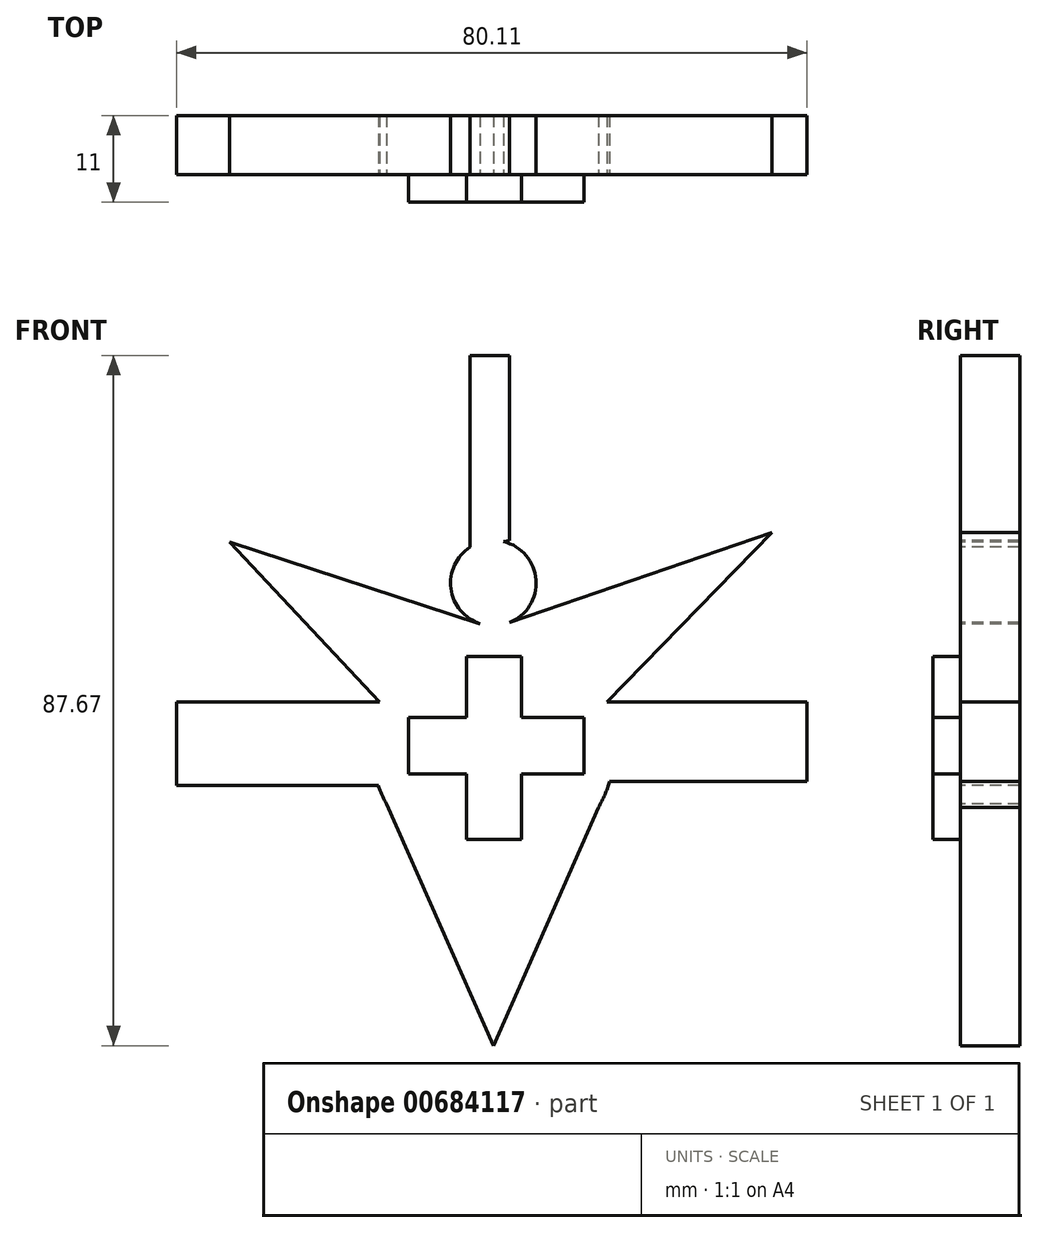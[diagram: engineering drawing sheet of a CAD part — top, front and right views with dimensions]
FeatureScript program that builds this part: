
annotation { "Feature Type Name" : "Feature", "Feature Type Description" : "" }
export const myFeature = defineFeature(function(context is Context, id is Id, definition is map)
    precondition{}
    {
        {
            var Q0;
            Q0=qCreatedBy(makeId("Front.planeOp"),FACE);
            var sketch = newSketch(context, id + "F0", { "sketchPlane" : qUnion([Q0])});
            skCircle(sketch, "E0", {"center": v(0, 0) * mm, "radius": 15.46 * mm});
            skSolve(sketch);
        }
        {
            var Q0;
            Q0=makeQuery(id+"F0.imprint","IMPRINT",FACE,{"disambiguationData":[TD([[makeQuery(id+"F0.imprint","IMPRINT",EDGE,{"derivedFrom":sQuery(id+"F0.wireOp",EDGE,"E0")}),1.0]])]});
            extrude(context, id + "F1", {"entities" : qUnion([Q0]), "oppositeDirection" : true, "depth" : 7.5 * mm, "offsetDistance" : 25 * mm});
        }
        {
            var Q0;
            Q0=qCreatedBy(makeId("Front.planeOp"),FACE);
            var sketch = newSketch(context, id + "F2", { "sketchPlane" : qUnion([Q0])});
            skLineSegment(sketch, "E1.bottom", {"start": v(-3.4, 11.35) * mm, "end": v(3.59, 11.35) * mm});
            skLineSegment(sketch, "E1.top", {"start": v(-3.4, -11.93) * mm, "end": v(3.59, -11.93) * mm});
            skLineSegment(sketch, "E1.left", {"start": v(-3.4, 11.35) * mm, "end": v(-3.4, 3.59) * mm});
            skLineSegment(sketch, "E1.right", {"start": v(3.59, 11.35) * mm, "end": v(3.59, 3.59) * mm});
            skLineSegment(sketch, "E2.bottom", {"start": v(-10.77, 3.59) * mm, "end": v(-3.4, 3.59) * mm});
            skLineSegment(sketch, "E2.top", {"start": v(-10.77, -3.59) * mm, "end": v(-3.4, -3.59) * mm});
            skLineSegment(sketch, "E2.left", {"start": v(-10.77, 3.59) * mm, "end": v(-10.77, -3.59) * mm});
            skLineSegment(sketch, "E2.right", {"start": v(11.54, 3.59) * mm, "end": v(11.54, -3.59) * mm});
            skLineSegment(sketch, "E3.trimOffspring", {"start": v(3.59, 3.59) * mm, "end": v(11.54, 3.59) * mm});
            skLineSegment(sketch, "E4.trimOffspring", {"start": v(-3.4, -3.59) * mm, "end": v(-3.4, -11.93) * mm});
            skLineSegment(sketch, "E5.trimOffspring", {"start": v(3.59, -3.59) * mm, "end": v(11.54, -3.59) * mm});
            skLineSegment(sketch, "E6.trimOffspring", {"start": v(3.59, -3.59) * mm, "end": v(3.59, -11.93) * mm});
            skSolve(sketch);
        }
        {
            var Q0;
            Q0 = qSketchRegion(id + "F2", true);
            extrude(context, id + "F3", {"entities" : qUnion([Q0]), "operationType" : NewBodyOperationType.ADD, "depth" : 3.5 * mm, "offsetDistance" : 25 * mm});
        }
        {
            var Q0;
            Q0=makeQuery(id+"F1.opExtrude","CAP_FACE",FACE,{"disambiguationData":[OSD([sQuery(id+"F0.wireOp",EDGE,"E0")])],"isStart":true});
            var sketch = newSketch(context, id + "F4", { "sketchPlane" : qUnion([Q0])});
            skLineSegment(sketch, "E7", {"start": v(-14.61, -5.06) * mm, "end": v(-40.25, -5.06) * mm});
            skLineSegment(sketch, "E8", {"start": v(-40.25, -5.06) * mm, "end": v(-40.25, 5.53) * mm});
            skLineSegment(sketch, "E9", {"start": v(-40.25, 5.53) * mm, "end": v(-14.44, 5.53) * mm});
            skSolve(sketch);
        }
        {
            var Q0;
            Q0 = qSketchRegion(id + "F4", true);
            var Q1;
            {var subQ0=sQuery(id+"F4.wireOp",EDGE,"E7");Q1=makeQuery(id+"F4.imprint","IMPRINT",FACE,{"disambiguationData":[TD([[makeQuery(id+"F4.imprint","IMPRINT",EDGE,{"derivedFrom":subQ0}),-1.0]])]});}
            extrude(context, id + "F5", {"entities" : qUnion([Q0, Q1]), "operationType" : NewBodyOperationType.ADD, "oppositeDirection" : true, "depth" : 7.5 * mm, "offsetDistance" : 25 * mm});
        }
        {
            var Q0;
            {var subQ0=sQuery(id+"F0.wireOp",EDGE,"E0");Q0=makeQuery(id+"F5.boolean.opBoolean","MERGE",FACE,{"derivedFrom":[makeQuery(id+"F1.opExtrude","CAP_FACE",FACE,{"disambiguationData":[OSD([subQ0])],"isStart":true}),makeQuery(id+"F5.opExtrude","CAP_FACE",FACE,{"disambiguationData":[OSD([subQ0,sQuery(id+"F4.wireOp",EDGE,"E7"),sQuery(id+"F4.wireOp",EDGE,"E8"),sQuery(id+"F4.wireOp",EDGE,"E9")])],"isStart":true})]});}
            var sketch = newSketch(context, id + "F6", { "sketchPlane" : qUnion([Q0])});
            skLineSegment(sketch, "E10", {"start": v(14.44, 5.53) * mm, "end": v(39.86, 5.53) * mm});
            skLineSegment(sketch, "E11", {"start": v(39.86, 5.53) * mm, "end": v(39.86, -4.56) * mm});
            skLineSegment(sketch, "E12", {"start": v(40.25, -4.56) * mm, "end": v(14.78, -4.56) * mm});
            skSolve(sketch);
        }
        {
            var Q0;
            Q0 = qSketchRegion(id + "F6", true);
            var Q1;
            {var subQ0=sQuery(id+"F6.wireOp",EDGE,"E10");Q1=makeQuery(id+"F6.imprint","IMPRINT",FACE,{"disambiguationData":[TD([[makeQuery(id+"F6.imprint","IMPRINT",EDGE,{"derivedFrom":subQ0}),-1.0]])]});}
            extrude(context, id + "F7", {"entities" : qUnion([Q0, Q1]), "operationType" : NewBodyOperationType.ADD, "oppositeDirection" : true, "depth" : 7.5 * mm, "offsetDistance" : 25 * mm});
        }
        {
            var Q0;
            {var subQ0=sQuery(id+"F0.wireOp",EDGE,"E0");Q0=makeQuery(id+"F7.boolean.opBoolean","MERGE",FACE,{"derivedFrom":[makeQuery(id+"F5.boolean.opBoolean","MERGE",FACE,{"derivedFrom":[makeQuery(id+"F1.opExtrude","CAP_FACE",FACE,{"disambiguationData":[OSD([subQ0])],"isStart":true}),makeQuery(id+"F5.opExtrude","CAP_FACE",FACE,{"disambiguationData":[OSD([subQ0,sQuery(id+"F4.wireOp",EDGE,"E7"),sQuery(id+"F4.wireOp",EDGE,"E8"),sQuery(id+"F4.wireOp",EDGE,"E9")])],"isStart":true})]}),makeQuery(id+"F7.opExtrude","CAP_FACE",FACE,{"disambiguationData":[OSD([subQ0,sQuery(id+"F6.wireOp",EDGE,"E10"),sQuery(id+"F6.wireOp",EDGE,"E11"),sQuery(id+"F6.wireOp",EDGE,"E12")])],"isStart":true})]});}
            var sketch = newSketch(context, id + "F8", { "sketchPlane" : qUnion([Q0])});
            skLineSegment(sketch, "E13", {"start": v(-14.61, -5.06) * mm, "end": v(0, -38.11) * mm});
            skLineSegment(sketch, "E14", {"start": v(0, -38.11) * mm, "end": v(14.78, -4.56) * mm});
            skSolve(sketch);
        }
        {
            var Q0;
            {var subQ0=sQuery(id+"F8.wireOp",EDGE,"E14");var subQ1=sQuery(id+"F8.wireOp",EDGE,"E13");var subQ2=makeQuery(id+"F8.imprint","INTERSECT",VERTEX,{"derivedFrom":[subQ1,subQ0]});Q0=makeQuery(id+"F8.imprint","IMPRINT",FACE,{"disambiguationData":[TD([[makeQuery(id+"F8.imprint","IMPRINT",EDGE,{"disambiguationData":[TD([[subQ2,1.0]])],"derivedFrom":subQ1}),1.0]])]});}
            extrude(context, id + "F9", {"entities" : qUnion([Q0]), "operationType" : NewBodyOperationType.ADD, "oppositeDirection" : true, "depth" : 7.5 * mm, "offsetDistance" : 25 * mm});
        }
        {
            var Q0;
            {var subQ0=sQuery(id+"F0.wireOp",EDGE,"E0");Q0=makeQuery(id+"F9.boolean.opBoolean","MERGE",FACE,{"derivedFrom":[makeQuery(id+"F7.boolean.opBoolean","MERGE",FACE,{"derivedFrom":[makeQuery(id+"F5.boolean.opBoolean","MERGE",FACE,{"derivedFrom":[makeQuery(id+"F1.opExtrude","CAP_FACE",FACE,{"disambiguationData":[OSD([subQ0])],"isStart":true}),makeQuery(id+"F5.opExtrude","CAP_FACE",FACE,{"disambiguationData":[OSD([subQ0,sQuery(id+"F4.wireOp",EDGE,"E7"),sQuery(id+"F4.wireOp",EDGE,"E8"),sQuery(id+"F4.wireOp",EDGE,"E9")])],"isStart":true})]}),makeQuery(id+"F7.opExtrude","CAP_FACE",FACE,{"disambiguationData":[OSD([subQ0,sQuery(id+"F6.wireOp",EDGE,"E10"),sQuery(id+"F6.wireOp",EDGE,"E11"),sQuery(id+"F6.wireOp",EDGE,"E12")])],"isStart":true})]}),makeQuery(id+"F9.opExtrude","CAP_FACE",FACE,{"disambiguationData":[OSD([subQ0,sQuery(id+"F8.wireOp",EDGE,"E13"),sQuery(id+"F8.wireOp",EDGE,"E14")])],"isStart":true})]});}
            var sketch = newSketch(context, id + "F10", { "sketchPlane" : qUnion([Q0])});
            skLineSegment(sketch, "E15.bottom", {"start": v(-1.68, 20.66) * mm, "end": v(1.46, 20.66) * mm});
            skLineSegment(sketch, "E15.top", {"start": v(-1.68, 15.4) * mm, "end": v(1.46, 15.4) * mm});
            skLineSegment(sketch, "E15.left", {"start": v(-1.68, 20.66) * mm, "end": v(-1.68, 15.4) * mm});
            skLineSegment(sketch, "E15.right", {"start": v(1.46, 20.66) * mm, "end": v(1.46, 15.4) * mm});
            skSolve(sketch);
        }
        {
            var Q0;
            Q0=makeQuery(id+"F10.imprint","IMPRINT",FACE,{"disambiguationData":[TD([[makeQuery(id+"F10.imprint","IMPRINT",EDGE,{"derivedFrom":sQuery(id+"F10.wireOp",EDGE,"E15.bottom")}),-1.0]])]});
            extrude(context, id + "F11", {"entities" : qUnion([Q0]), "operationType" : NewBodyOperationType.ADD, "oppositeDirection" : true, "depth" : 7.5 * mm, "offsetDistance" : 25 * mm});
        }
        {
            var Q0;
            {var subQ0=sQuery(id+"F0.wireOp",EDGE,"E0");Q0=makeQuery(id+"F11.boolean.opBoolean","MERGE",FACE,{"derivedFrom":[makeQuery(id+"F9.boolean.opBoolean","MERGE",FACE,{"derivedFrom":[makeQuery(id+"F7.boolean.opBoolean","MERGE",FACE,{"derivedFrom":[makeQuery(id+"F5.boolean.opBoolean","MERGE",FACE,{"derivedFrom":[makeQuery(id+"F1.opExtrude","CAP_FACE",FACE,{"disambiguationData":[OSD([subQ0])],"isStart":true}),makeQuery(id+"F5.opExtrude","CAP_FACE",FACE,{"disambiguationData":[OSD([subQ0,sQuery(id+"F4.wireOp",EDGE,"E7"),sQuery(id+"F4.wireOp",EDGE,"E8"),sQuery(id+"F4.wireOp",EDGE,"E9")])],"isStart":true})]}),makeQuery(id+"F7.opExtrude","CAP_FACE",FACE,{"disambiguationData":[OSD([subQ0,sQuery(id+"F6.wireOp",EDGE,"E10"),sQuery(id+"F6.wireOp",EDGE,"E11"),sQuery(id+"F6.wireOp",EDGE,"E12")])],"isStart":true})]}),makeQuery(id+"F9.opExtrude","CAP_FACE",FACE,{"disambiguationData":[OSD([subQ0,sQuery(id+"F8.wireOp",EDGE,"E13"),sQuery(id+"F8.wireOp",EDGE,"E14")])],"isStart":true})]}),makeQuery(id+"F11.opExtrude","CAP_FACE",FACE,{"disambiguationData":[OSD([subQ0,sQuery(id+"F10.wireOp",EDGE,"E15.bottom"),sQuery(id+"F10.wireOp",EDGE,"E15.top"),sQuery(id+"F10.wireOp",EDGE,"E15.left"),sQuery(id+"F10.wireOp",EDGE,"E15.right")])],"isStart":true})]});}
            var sketch = newSketch(context, id + "F12", { "sketchPlane" : qUnion([Q0])});
            skCircle(sketch, "E16", {"center": v(0, 20.66) * mm, "radius": 5.43 * mm});
            skSolve(sketch);
        }
        {
            var Q0;
            {var subQ5=makeQuery(id+"F11.opExtrude","CAP_EDGE",EDGE,{"disambiguationData":[OSD([sQuery(id+"F10.wireOp",EDGE,"E15.bottom")])],"isStart":true});Q0=makeQuery(id+"F12.imprint","IMPRINT",FACE,{"disambiguationData":[TD([[makeQuery(id+"F12.imprint","IMPRINT",EDGE,{"derivedFrom":subQ5}),1.0]])]});}
            extrude(context, id + "F13", {"entities" : qUnion([Q0]), "operationType" : NewBodyOperationType.ADD, "oppositeDirection" : true, "depth" : 7.5 * mm, "offsetDistance" : 25 * mm});
        }
        {
            var Q0;
            {var subQ0=sQuery(id+"F10.wireOp",EDGE,"E15.right");var subQ1=sQuery(id+"F10.wireOp",EDGE,"E15.left");var subQ2=sQuery(id+"F10.wireOp",EDGE,"E15.bottom");var subQ3=sQuery(id+"F0.wireOp",EDGE,"E0");Q0=makeQuery(id+"F13.boolean.opBoolean","MERGE",FACE,{"derivedFrom":[makeQuery(id+"F11.boolean.opBoolean","MERGE",FACE,{"derivedFrom":[makeQuery(id+"F9.boolean.opBoolean","MERGE",FACE,{"derivedFrom":[makeQuery(id+"F7.boolean.opBoolean","MERGE",FACE,{"derivedFrom":[makeQuery(id+"F5.boolean.opBoolean","MERGE",FACE,{"derivedFrom":[makeQuery(id+"F1.opExtrude","CAP_FACE",FACE,{"disambiguationData":[OSD([subQ3])],"isStart":true}),makeQuery(id+"F5.opExtrude","CAP_FACE",FACE,{"disambiguationData":[OSD([subQ3,sQuery(id+"F4.wireOp",EDGE,"E7"),sQuery(id+"F4.wireOp",EDGE,"E8"),sQuery(id+"F4.wireOp",EDGE,"E9")])],"isStart":true})]}),makeQuery(id+"F7.opExtrude","CAP_FACE",FACE,{"disambiguationData":[OSD([subQ3,sQuery(id+"F6.wireOp",EDGE,"E10"),sQuery(id+"F6.wireOp",EDGE,"E11"),sQuery(id+"F6.wireOp",EDGE,"E12")])],"isStart":true})]}),makeQuery(id+"F9.opExtrude","CAP_FACE",FACE,{"disambiguationData":[OSD([subQ3,sQuery(id+"F8.wireOp",EDGE,"E13"),sQuery(id+"F8.wireOp",EDGE,"E14")])],"isStart":true})]}),makeQuery(id+"F11.opExtrude","CAP_FACE",FACE,{"disambiguationData":[OSD([subQ3,subQ2,sQuery(id+"F10.wireOp",EDGE,"E15.top"),subQ1,subQ0])],"isStart":true})]}),makeQuery(id+"F13.opExtrude","CAP_FACE",FACE,{"disambiguationData":[OSD([subQ2,subQ1,subQ0,sQuery(id+"F12.wireOp",EDGE,"E16")])],"isStart":true})]});}
            var sketch = newSketch(context, id + "F14", { "sketchPlane" : qUnion([Q0])});
            skLineSegment(sketch, "E17", {"start": v(-1.46, 15.4) * mm, "end": v(-34.54, 28.08) * mm});
            skLineSegment(sketch, "E18", {"start": v(-34.57, 28.03) * mm, "end": v(-14.44, 5.53) * mm});
            skLineSegment(sketch, "E19", {"start": v(1.46, 15.42) * mm, "end": v(35.4, 27.06) * mm});
            skLineSegment(sketch, "E20", {"start": v(35.4, 27.06) * mm, "end": v(14.44, 5.53) * mm});
            skSolve(sketch);
        }
        {
            var Q0;
            {var subQ10=sQuery(id+"F14.wireOp",EDGE,"E20");Q0=makeQuery(id+"F14.imprint","IMPRINT",FACE,{"disambiguationData":[TD([[makeQuery(id+"F14.imprint","IMPRINT",EDGE,{"derivedFrom":subQ10}),-1.0]])]});}
            extrude(context, id + "F15", {"entities" : qUnion([Q0]), "operationType" : NewBodyOperationType.ADD, "oppositeDirection" : true, "depth" : 7.5 * mm, "offsetDistance" : 25 * mm});
        }
        {
            var Q0;
            {var subQ0=sQuery(id+"F12.wireOp",EDGE,"E16");var subQ1=sQuery(id+"F10.wireOp",EDGE,"E15.right");var subQ2=sQuery(id+"F0.wireOp",EDGE,"E0");var subQ3=sQuery(id+"F10.wireOp",EDGE,"E15.left");var subQ4=sQuery(id+"F10.wireOp",EDGE,"E15.bottom");Q0=makeQuery(id+"F15.boolean.opBoolean","MERGE",FACE,{"derivedFrom":[makeQuery(id+"F13.boolean.opBoolean","MERGE",FACE,{"derivedFrom":[makeQuery(id+"F11.boolean.opBoolean","MERGE",FACE,{"derivedFrom":[makeQuery(id+"F9.boolean.opBoolean","MERGE",FACE,{"derivedFrom":[makeQuery(id+"F7.boolean.opBoolean","MERGE",FACE,{"derivedFrom":[makeQuery(id+"F5.boolean.opBoolean","MERGE",FACE,{"derivedFrom":[makeQuery(id+"F1.opExtrude","CAP_FACE",FACE,{"disambiguationData":[OSD([subQ2])],"isStart":true}),makeQuery(id+"F5.opExtrude","CAP_FACE",FACE,{"disambiguationData":[OSD([subQ2,sQuery(id+"F4.wireOp",EDGE,"E7"),sQuery(id+"F4.wireOp",EDGE,"E8"),sQuery(id+"F4.wireOp",EDGE,"E9")])],"isStart":true})]}),makeQuery(id+"F7.opExtrude","CAP_FACE",FACE,{"disambiguationData":[OSD([subQ2,sQuery(id+"F6.wireOp",EDGE,"E10"),sQuery(id+"F6.wireOp",EDGE,"E11"),sQuery(id+"F6.wireOp",EDGE,"E12")])],"isStart":true})]}),makeQuery(id+"F9.opExtrude","CAP_FACE",FACE,{"disambiguationData":[OSD([subQ2,sQuery(id+"F8.wireOp",EDGE,"E13"),sQuery(id+"F8.wireOp",EDGE,"E14")])],"isStart":true})]}),makeQuery(id+"F11.opExtrude","CAP_FACE",FACE,{"disambiguationData":[OSD([subQ2,subQ4,sQuery(id+"F10.wireOp",EDGE,"E15.top"),subQ3,subQ1])],"isStart":true})]}),makeQuery(id+"F13.opExtrude","CAP_FACE",FACE,{"disambiguationData":[OSD([subQ4,subQ3,subQ1,subQ0])],"isStart":true})]}),makeQuery(id+"F15.opExtrude","CAP_FACE",FACE,{"disambiguationData":[OSD([subQ2,subQ1,subQ0,sQuery(id+"F14.wireOp",EDGE,"E19"),sQuery(id+"F14.wireOp",EDGE,"E20")])],"isStart":true})]});}
            var sketch = newSketch(context, id + "F16", { "sketchPlane" : qUnion([Q0])});
            skLineSegment(sketch, "E21", {"start": v(-1.68, 15.49) * mm, "end": v(-35.1, 26.37) * mm});
            skLineSegment(sketch, "E22", {"start": v(-34.82, 27.25) * mm, "end": v(-14.44, 5.53) * mm});
            skSolve(sketch);
        }
        {
            var Q0;
            {var subQ0=sQuery(id+"F10.wireOp",EDGE,"E15.top");Q0=makeQuery(id+"F16.imprint","IMPRINT",FACE,{"disambiguationData":[TD([[makeQuery(id+"F16.imprint","IMPRINT",EDGE,{"derivedFrom":makeQuery(id+"F11.opExtrude","CAP_EDGE",EDGE,{"disambiguationData":[OSD([subQ0])],"isStart":true})}),-1.0]])]});}
            extrude(context, id + "F17", {"entities" : qUnion([Q0]), "operationType" : NewBodyOperationType.ADD, "oppositeDirection" : true, "depth" : 7.5 * mm, "offsetDistance" : 25 * mm});
        }
        {
            var Q0;
            Q0=qCreatedBy(makeId("Front.planeOp"),FACE);
            var sketch = newSketch(context, id + "F18", { "sketchPlane" : qUnion([Q0])});
            skLineSegment(sketch, "E23.bottom", {"start": v(-2.4, 26.21) * mm, "end": v(3.1, 26.21) * mm});
            skLineSegment(sketch, "E23.top", {"start": v(-2.4, 55.06) * mm, "end": v(3.1, 55.06) * mm});
            skLineSegment(sketch, "E23.left", {"start": v(-2.4, 26.21) * mm, "end": v(-2.4, 55.06) * mm});
            skLineSegment(sketch, "E23.right", {"start": v(3.1, 26.21) * mm, "end": v(3.1, 55.06) * mm});
            skSolve(sketch);
        }
        {
            var Q0;
            Q0=makeQuery(id+"F18.imprint","IMPRINT",FACE,{"disambiguationData":[TD([[makeQuery(id+"F18.imprint","IMPRINT",EDGE,{"derivedFrom":sQuery(id+"F18.wireOp",EDGE,"E23.bottom")}),1.0]])]});
            extrude(context, id + "F19", {"entities" : qUnion([Q0]), "oppositeDirection" : true, "depth" : 7.5 * mm, "offsetDistance" : 25 * mm});
        }
        {
            var Q0;
            Q0=makeQuery(id+"F19.opExtrude","SWEPT_BODY",BODY,{"disambiguationData":[OSD([sQuery(id+"F18.wireOp",EDGE,"E23.bottom"),sQuery(id+"F18.wireOp",EDGE,"E23.top"),sQuery(id+"F18.wireOp",EDGE,"E23.left"),sQuery(id+"F18.wireOp",EDGE,"E23.right")])]});
            deleteBodies(context, id + "F20", {"entities" : qUnion([Q0])});
        }
        {
            var Q0;
            {var subQ0=sQuery(id+"F10.wireOp",EDGE,"E15.left");var subQ1=sQuery(id+"F10.wireOp",EDGE,"E15.top");var subQ2=sQuery(id+"F0.wireOp",EDGE,"E0");var subQ3=sQuery(id+"F12.wireOp",EDGE,"E16");var subQ4=sQuery(id+"F10.wireOp",EDGE,"E15.right");var subQ5=sQuery(id+"F10.wireOp",EDGE,"E15.bottom");Q0=makeQuery(id+"F17.boolean.opBoolean","MERGE",FACE,{"derivedFrom":[makeQuery(id+"F15.boolean.opBoolean","MERGE",FACE,{"derivedFrom":[makeQuery(id+"F13.boolean.opBoolean","MERGE",FACE,{"derivedFrom":[makeQuery(id+"F11.boolean.opBoolean","MERGE",FACE,{"derivedFrom":[makeQuery(id+"F9.boolean.opBoolean","MERGE",FACE,{"derivedFrom":[makeQuery(id+"F7.boolean.opBoolean","MERGE",FACE,{"derivedFrom":[makeQuery(id+"F5.boolean.opBoolean","MERGE",FACE,{"derivedFrom":[makeQuery(id+"F1.opExtrude","CAP_FACE",FACE,{"disambiguationData":[OSD([subQ2])],"isStart":true}),makeQuery(id+"F5.opExtrude","CAP_FACE",FACE,{"disambiguationData":[OSD([subQ2,sQuery(id+"F4.wireOp",EDGE,"E7"),sQuery(id+"F4.wireOp",EDGE,"E8"),sQuery(id+"F4.wireOp",EDGE,"E9")])],"isStart":true})]}),makeQuery(id+"F7.opExtrude","CAP_FACE",FACE,{"disambiguationData":[OSD([subQ2,sQuery(id+"F6.wireOp",EDGE,"E10"),sQuery(id+"F6.wireOp",EDGE,"E11"),sQuery(id+"F6.wireOp",EDGE,"E12")])],"isStart":true})]}),makeQuery(id+"F9.opExtrude","CAP_FACE",FACE,{"disambiguationData":[OSD([subQ2,sQuery(id+"F8.wireOp",EDGE,"E13"),sQuery(id+"F8.wireOp",EDGE,"E14")])],"isStart":true})]}),makeQuery(id+"F11.opExtrude","CAP_FACE",FACE,{"disambiguationData":[OSD([subQ2,subQ5,subQ1,subQ0,subQ4])],"isStart":true})]}),makeQuery(id+"F13.opExtrude","CAP_FACE",FACE,{"disambiguationData":[OSD([subQ5,subQ0,subQ4,subQ3])],"isStart":true})]}),makeQuery(id+"F15.opExtrude","CAP_FACE",FACE,{"disambiguationData":[OSD([subQ2,subQ4,subQ3,sQuery(id+"F14.wireOp",EDGE,"E19"),sQuery(id+"F14.wireOp",EDGE,"E20")])],"isStart":true})]}),makeQuery(id+"F17.opExtrude","CAP_FACE",FACE,{"disambiguationData":[OSD([subQ2,subQ1,subQ0,sQuery(id+"F16.wireOp",EDGE,"E21"),sQuery(id+"F16.wireOp",EDGE,"E22")])],"isStart":true})]});}
            var sketch = newSketch(context, id + "F21", { "sketchPlane" : qUnion([Q0])});
            skLineSegment(sketch, "E24", {"start": v(-2.96, 25.21) * mm, "end": v(-2.96, 49.56) * mm});
            skLineSegment(sketch, "E25", {"start": v(-2.96, 49.56) * mm, "end": v(2.06, 49.56) * mm});
            skLineSegment(sketch, "E26", {"start": v(2.06, 49.56) * mm, "end": v(2.06, 25.68) * mm});
            skLineSegment(sketch, "E27", {"start": v(2.17, 26.07) * mm, "end": v(-2.96, 25.21) * mm});
            skSolve(sketch);
        }
        {
            var Q0;
            {var subQ6=sQuery(id+"F21.wireOp",EDGE,"E24");Q0=makeQuery(id+"F21.imprint","IMPRINT",FACE,{"disambiguationData":[TD([[makeQuery(id+"F21.imprint","IMPRINT",EDGE,{"derivedFrom":subQ6}),-1.0]])]});}
            extrude(context, id + "F22", {"entities" : qUnion([Q0]), "operationType" : NewBodyOperationType.ADD, "oppositeDirection" : true, "depth" : 7.5 * mm, "offsetDistance" : 25 * mm});
        }
    });
